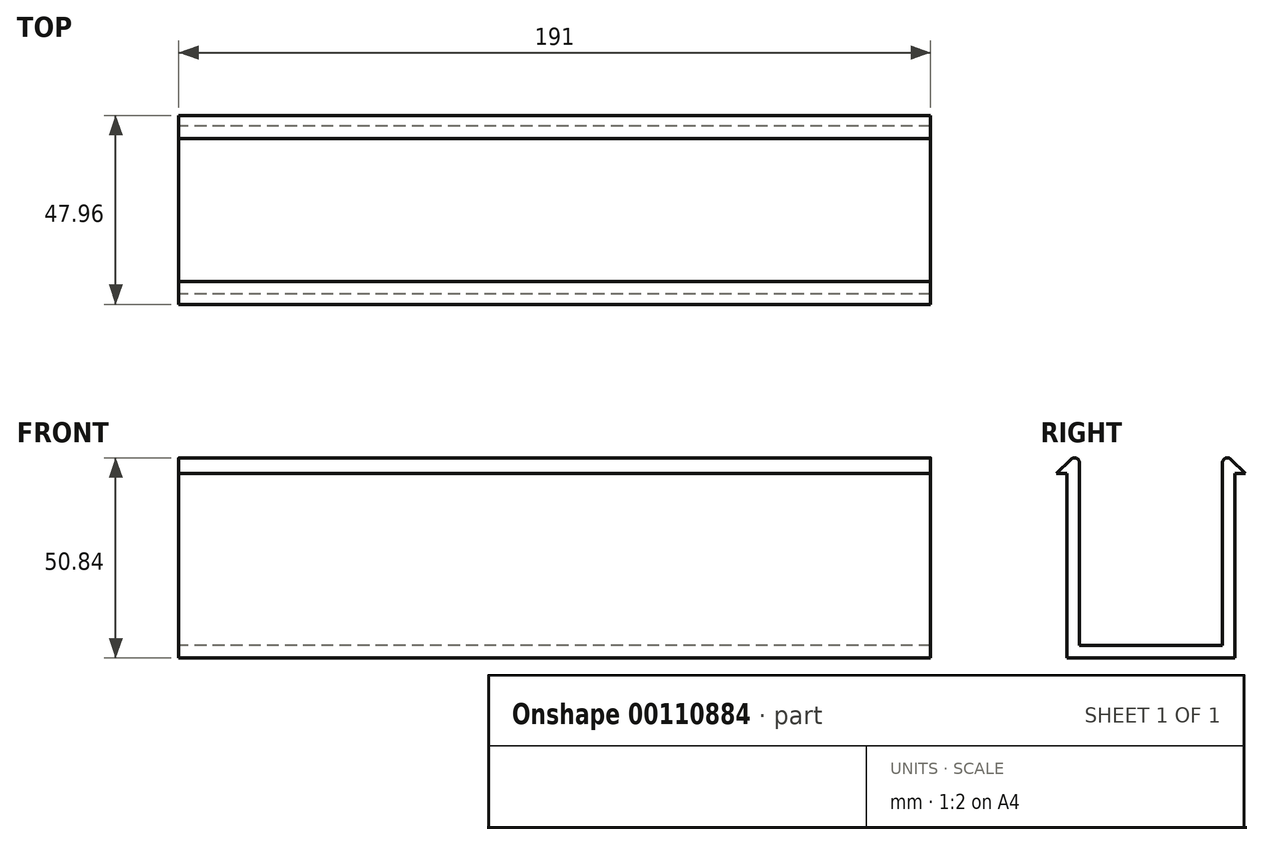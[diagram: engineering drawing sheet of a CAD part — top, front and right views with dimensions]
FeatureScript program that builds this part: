
annotation { "Feature Type Name" : "Feature", "Feature Type Description" : "" }
export const myFeature = defineFeature(function(context is Context, id is Id, definition is map)
    precondition{}
    {
        {
            var Q0;
            Q0=qCreatedBy(makeId("Right.planeOp"),FACE);
            var sketch = newSketch(context, id + "F0", { "sketchPlane" : qUnion([Q0])});
            skLineSegment(sketch, "E0", {"start": v(0, 0) * mm, "end": v(21.34, 0) * mm});
            skLineSegment(sketch, "E1", {"start": v(21.34, 0) * mm, "end": v(21.34, 46.82) * mm});
            skLineSegment(sketch, "E2", {"start": v(18.16, 49.57) * mm, "end": v(18.16, 3.18) * mm});
            skLineSegment(sketch, "E3", {"start": v(18.16, 3.18) * mm, "end": v(0, 3.17) * mm});
            skLineSegment(sketch, "E4", {"start": v(19.75, 50.8) * mm, "end": v(19.75, 46.82) * mm, "construction": true});
            skLineSegment(sketch, "E5", {"start": v(21.34, 46.82) * mm, "end": v(23.98, 46.82) * mm});
            skLineSegment(sketch, "E6", {"start": v(23.98, 46.82) * mm, "end": v(20.33, 50.47) * mm});
            skArc(sketch, "E7", {"start": v(19.75, 50.8) * mm, "mid": v(18.65, 50.57) * mm, "end": v(18.16, 49.57) * mm});
            skPoint(sketch, "E8.orphan", {"position": v(18.16, 50.8) * mm});
            skArc(sketch, "E9", {"start": v(20.33, 50.47) * mm, "mid": v(18.94, 50.74) * mm, "end": v(18.16, 49.57) * mm});
            skPoint(sketch, "E10.orphan", {"position": v(21.34, 50.8) * mm});
            skLineSegment(sketch, "E11", {"start": v(0, 0) * mm, "end": v(0, 3.17) * mm});
            skArc(sketch, "E12.MirrorCS", {"start": v(-19.75, 50.8) * mm, "mid": v(-18.65, 50.57) * mm, "end": v(-18.16, 49.57) * mm});
            skArc(sketch, "E13.MirrorCS", {"start": v(-20.33, 50.47) * mm, "mid": v(-18.94, 50.74) * mm, "end": v(-18.16, 49.57) * mm});
            skLineSegment(sketch, "E14.MirrorCS", {"start": v(-23.98, 46.82) * mm, "end": v(-20.33, 50.47) * mm});
            skLineSegment(sketch, "E15.MirrorCS", {"start": v(-19.75, 50.8) * mm, "end": v(-19.75, 46.82) * mm, "construction": true});
            skLineSegment(sketch, "E16.MirrorCS", {"start": v(-21.34, 46.82) * mm, "end": v(-23.98, 46.82) * mm});
            skLineSegment(sketch, "E17.MirrorCS", {"start": v(-18.16, 49.57) * mm, "end": v(-18.16, 3.18) * mm});
            skLineSegment(sketch, "E18.MirrorCS", {"start": v(-18.16, 3.18) * mm, "end": v(0, 3.17) * mm});
            skLineSegment(sketch, "E19.MirrorCS", {"start": v(-21.34, 0) * mm, "end": v(-21.34, 46.82) * mm});
            skLineSegment(sketch, "E20.MirrorCS", {"start": v(0, 0) * mm, "end": v(-21.34, 0) * mm});
            skSolve(sketch);
        }
        {
            var Q0;
            Q0=makeQuery(id+"F0.imprint","IMPRINT",FACE,{"disambiguationData":[TD([[makeQuery(id+"F0.imprint","IMPRINT",EDGE,{"derivedFrom":sQuery(id+"F0.wireOp",EDGE,"E11")}),1.0]])]});
            var Q1;
            Q1=makeQuery(id+"F0.imprint","IMPRINT",FACE,{"disambiguationData":[TD([[makeQuery(id+"F0.imprint","IMPRINT",EDGE,{"derivedFrom":sQuery(id+"F0.wireOp",EDGE,"E0")}),1.0]])]});
            extrude(context, id + "F1", {"entities" : qUnion([Q0, Q1]), "endBound" : BoundingType.SYMMETRIC, "depth" : 191 * mm});
        }
    });
